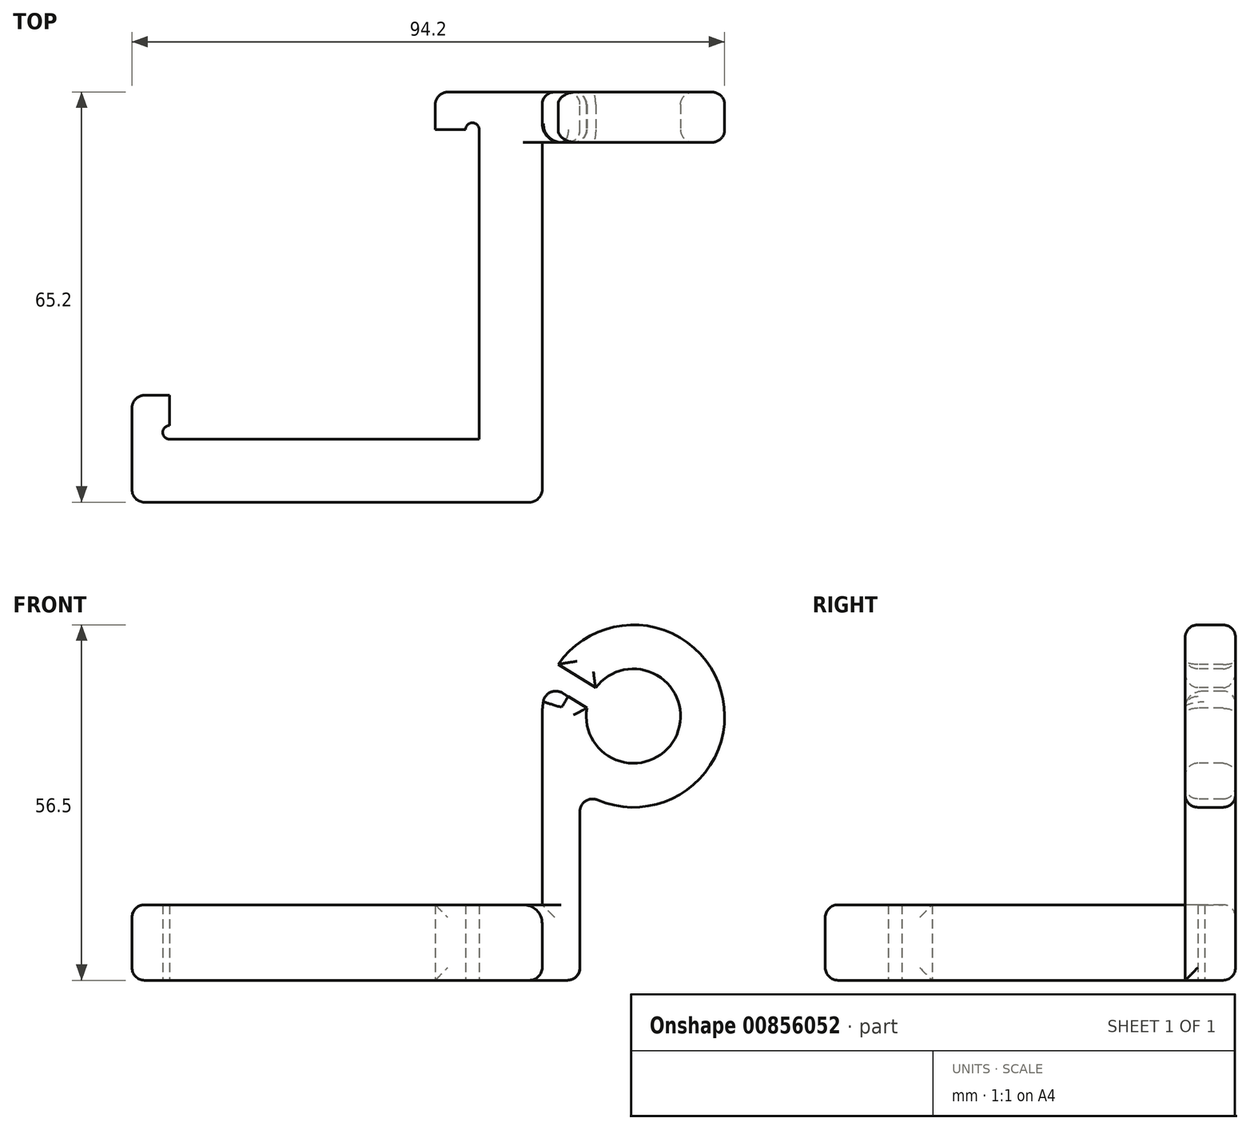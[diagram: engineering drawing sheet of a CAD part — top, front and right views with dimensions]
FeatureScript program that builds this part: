
annotation { "Feature Type Name" : "Feature", "Feature Type Description" : "" }
export const myFeature = defineFeature(function(context is Context, id is Id, definition is map)
    precondition{}
    {
        {
            var Q0;
            Q0=qCreatedBy(makeId("Top.planeOp"),FACE);
            var sketch = newSketch(context, id + "F0", { "sketchPlane" : qUnion([Q0])});
            skLineSegment(sketch, "E0.bottom", {"start": v(0, 0) * mm, "end": v(65.2, 0) * mm});
            skLineSegment(sketch, "E0.top", {"start": v(0, 17) * mm, "end": v(6, 17) * mm});
            skLineSegment(sketch, "E0.left", {"start": v(0, 0) * mm, "end": v(0, 17) * mm});
            skLineSegment(sketch, "E0.right", {"start": v(65.2, 0) * mm, "end": v(65.2, 65.2) * mm});
            skLineSegment(sketch, "E1.top", {"start": v(6, 10) * mm, "end": v(55.2, 10) * mm});
            skLineSegment(sketch, "E1.left", {"start": v(6, 17) * mm, "end": v(6, 10) * mm});
            skLineSegment(sketch, "E1.right", {"start": v(55.2, 59.2) * mm, "end": v(55.2, 10) * mm});
            skLineSegment(sketch, "E2.bottom", {"start": v(65.2, 65.2) * mm, "end": v(48.2, 65.2) * mm});
            skLineSegment(sketch, "E2.top", {"start": v(55.2, 59.2) * mm, "end": v(48.2, 59.2) * mm});
            skLineSegment(sketch, "E2.left", {"start": v(65.2, 65.2) * mm, "end": v(65.2, 59.2) * mm});
            skLineSegment(sketch, "E2.right", {"start": v(48.2, 65.2) * mm, "end": v(48.2, 59.2) * mm});
            skSolve(sketch);
        }
        {
            var Q0;
            Q0=qSketchRegion(id+"F0",true);
            extrude(context, id + "F1", {"entities" : qUnion([Q0]), "depth" : 12 * mm, "offsetDistance" : 25 * mm});
        }
        {
            var Q0;
            Q0=qCreatedBy(makeId("Top.planeOp"),FACE);
            var sketch = newSketch(context, id + "F2", { "sketchPlane" : qUnion([Q0])});
            skCircle(sketch, "E3", {"center": v(6, 11.1) * mm, "radius": 1.1 * mm});
            skCircle(sketch, "E4", {"center": v(54.1, 59.2) * mm, "radius": 1.1 * mm});
            skSolve(sketch);
        }
        {
            var Q0;
            Q0=qSketchRegion(id+"F2",true);
            extrude(context, id + "F3", {"entities" : qUnion([Q0]), "operationType" : NewBodyOperationType.REMOVE, "endBound" : BoundingType.THROUGH_ALL, "depth" : 25 * mm, "offsetDistance" : 25 * mm});
        }
        {
            var Q0;
            Q0=makeQuery(id+"F1.opExtrude","SWEPT_FACE",FACE,{"disambiguationData":[OSD([sQuery(id+"F0.wireOp",EDGE,"E0.right"),sQuery(id+"F0.wireOp",EDGE,"E2.left")])]});
            var sketch = newSketch(context, id + "F4", { "sketchPlane" : qUnion([Q0])});
            skLineSegment(sketch, "E5.bottom", {"start": v(65.2, 0) * mm, "end": v(57.2, 0) * mm});
            skLineSegment(sketch, "E5.top", {"start": v(65.2, 42) * mm, "end": v(57.2, 42) * mm});
            skLineSegment(sketch, "E5.left", {"start": v(65.2, 0) * mm, "end": v(65.2, 42) * mm});
            skLineSegment(sketch, "E5.right", {"start": v(57.2, 0) * mm, "end": v(57.2, 42) * mm});
            skSolve(sketch);
        }
        {
            var Q0;
            Q0 = qSketchRegion(id + "F4", true);
            extrude(context, id + "F5", {"entities" : qUnion([Q0]), "operationType" : NewBodyOperationType.ADD, "depth" : 6 * mm, "offsetDistance" : 25 * mm});
        }
        {
            var Q0;
            Q0=makeQuery(id+"F5.opExtrude","SWEPT_FACE",FACE,{"disambiguationData":[OSD([sQuery(id+"F4.wireOp",EDGE,"E5.right")])]});
            var sketch = newSketch(context, id + "F6", { "sketchPlane" : qUnion([Q0])});
            skArc(sketch, "E6", {"start": v(66.12, 47.1) * mm, "mid": v(92.56, 35.3) * mm, "end": v(67.75, 50.2) * mm});
            skArc(sketch, "E7", {"start": v(72.3, 43.25) * mm, "mid": v(86.6, 39.04) * mm, "end": v(73.7, 46.5) * mm});
            skLineSegment(sketch, "E8", {"start": v(72.3, 43.25) * mm, "end": v(66.12, 47.1) * mm});
            skLineSegment(sketch, "E9", {"start": v(73.7, 46.5) * mm, "end": v(67.75, 50.2) * mm});
            skSolve(sketch);
        }
        {
            var Q0;
            Q0 = qSketchRegion(id + "F6", true);
            var Q1;
            Q1=makeQuery(id+"F5.boolean.opBoolean","MERGE",FACE,{"derivedFrom":[makeQuery(id+"F1.opExtrude","SWEPT_FACE",FACE,{"disambiguationData":[OSD([sQuery(id+"F0.wireOp",EDGE,"E2.bottom")])]}),makeQuery(id+"F5.opExtrude","SWEPT_FACE",FACE,{"disambiguationData":[OSD([sQuery(id+"F4.wireOp",EDGE,"E5.left")])]})]});
            extrude(context, id + "F7", {"entities" : qUnion([Q0]), "operationType" : NewBodyOperationType.ADD, "endBound" : BoundingType.UP_TO_SURFACE, "oppositeDirection" : true, "depth" : 6 * mm, "endBoundEntityFace" : qUnion([Q1]), "offsetDistance" : 25 * mm});
        }
        {
            var Q0;
            {var subQ0=sQuery(id+"F0.wireOp",EDGE,"E2.left");var subQ1=sQuery(id+"F0.wireOp",EDGE,"E0.right");Q0=makeQuery(id+"F5.boolean.opBoolean","SPLIT",EDGE,{"disambiguationData":[topologyDisambiguationEdgeConnected([makeQuery(id+"F5.opExtrude","CAP_FACE",FACE,{"disambiguationData":[OSD([sQuery(id+"F4.wireOp",EDGE,"E5.bottom"),sQuery(id+"F4.wireOp",EDGE,"E5.top"),sQuery(id+"F4.wireOp",EDGE,"E5.left"),sQuery(id+"F4.wireOp",EDGE,"E5.right")])],"isStart":true})])],"derivedFrom":makeQuery(id+"F1.opExtrude","CAP_EDGE",EDGE,{"disambiguationData":[OSD([subQ1,subQ0])],"isStart":false})});}
            fillet(context, id + "F8", {"entities" : qUnion([Q0]), "radius" : 3 * mm, "tangentPropagation" : true, "allowEdgeOverflow" : false});
        }
        {
            var Q0;
            {var subQ0=sQuery(id+"F4.wireOp",EDGE,"E5.right");var subQ1=sQuery(id+"F0.wireOp",EDGE,"E2.left");var subQ2=sQuery(id+"F0.wireOp",EDGE,"E0.right");Q0=makeQuery(id+"F8.opFillet","TWEAK_EDGE",EDGE,{"derivedFrom":[makeQuery(id+"F5.boolean.opBoolean","TWEAK_VERTEX",VERTEX,{"derivedFrom":[makeQuery(id+"F1.opExtrude","SWEPT_FACE",FACE,{"disambiguationData":[OSD([subQ2,subQ1])]}),makeQuery(id+"F1.opExtrude","CAP_FACE",FACE,{"disambiguationData":[OSD([sQuery(id+"F0.wireOp",EDGE,"E0.bottom"),sQuery(id+"F0.wireOp",EDGE,"E0.top"),sQuery(id+"F0.wireOp",EDGE,"E0.left"),subQ2,sQuery(id+"F0.wireOp",EDGE,"E1.top"),sQuery(id+"F0.wireOp",EDGE,"E1.left"),sQuery(id+"F0.wireOp",EDGE,"E1.right"),sQuery(id+"F0.wireOp",EDGE,"E2.bottom"),sQuery(id+"F0.wireOp",EDGE,"E2.top"),subQ1,sQuery(id+"F0.wireOp",EDGE,"E2.right")])],"isStart":false}),makeQuery(id+"F5.opExtrude","CAP_FACE",FACE,{"disambiguationData":[OSD([sQuery(id+"F4.wireOp",EDGE,"E5.bottom"),sQuery(id+"F4.wireOp",EDGE,"E5.top"),sQuery(id+"F4.wireOp",EDGE,"E5.left"),subQ0])],"isStart":true}),makeQuery(id+"F5.opExtrude","SWEPT_FACE",FACE,{"disambiguationData":[OSD([subQ0])]})]})]});}
            var Q1;
            {var subQ0=sQuery(id+"F4.wireOp",EDGE,"E5.right");Q1=makeQuery(id+"F5.boolean.opBoolean","SPLIT",EDGE,{"disambiguationData":[topologyDisambiguationEdgeConnected([makeQuery(id+"F1.opExtrude","SWEPT_FACE",FACE,{"disambiguationData":[OSD([sQuery(id+"F0.wireOp",EDGE,"E0.right"),sQuery(id+"F0.wireOp",EDGE,"E2.left")])]})])],"derivedFrom":makeQuery(id+"F5.opExtrude","CAP_EDGE",EDGE,{"disambiguationData":[OSD([subQ0])],"isStart":true})});}
            fillet(context, id + "F9", {"entities" : qUnion([Q0, Q1]), "radius" : 3 * mm, "tangentPropagation" : true, "allowEdgeOverflow" : false});
        }
        {
            var Q0;
            Q0=makeQuery(id+"F1.opExtrude","SWEPT_FACE",FACE,{"disambiguationData":[OSD([sQuery(id+"F0.wireOp",EDGE,"E0.left")])]});
            var Q1;
            Q1=makeQuery(id+"F1.opExtrude","SWEPT_FACE",FACE,{"disambiguationData":[OSD([sQuery(id+"F0.wireOp",EDGE,"E0.bottom")])]});
            var Q2;
            {var subQ0=sQuery(id+"F4.wireOp",EDGE,"E5.left");var subQ1=sQuery(id+"F0.wireOp",EDGE,"E2.bottom");Q2=makeQuery(id+"F7.boolean.opBoolean","MERGE",FACE,{"derivedFrom":[makeQuery(id+"F5.boolean.opBoolean","MERGE",FACE,{"derivedFrom":[makeQuery(id+"F1.opExtrude","SWEPT_FACE",FACE,{"disambiguationData":[OSD([subQ1])]}),makeQuery(id+"F5.opExtrude","SWEPT_FACE",FACE,{"disambiguationData":[OSD([subQ0])]})]}),makeQuery(id+"F7.opExtrude","CAP_FACE",FACE,{"disambiguationData":[OSD([subQ1,subQ0])],"isStart":false})]});}
            var Q3;
            {var subQ0=sQuery(id+"F4.wireOp",EDGE,"E5.right");Q3=makeQuery(id+"F5.boolean.opBoolean","SPLIT",EDGE,{"disambiguationData":[topologyDisambiguationEdgeConnected([makeQuery(id+"F5.opExtrude","CAP_FACE",FACE,{"disambiguationData":[OSD([sQuery(id+"F4.wireOp",EDGE,"E5.bottom"),sQuery(id+"F4.wireOp",EDGE,"E5.top"),sQuery(id+"F4.wireOp",EDGE,"E5.left"),subQ0])],"isStart":true})])],"derivedFrom":makeQuery(id+"F5.opExtrude","CAP_EDGE",EDGE,{"disambiguationData":[OSD([subQ0])],"isStart":true})});}
            var Q4;
            Q4=makeQuery(id+"F5.opExtrude","CAP_EDGE",EDGE,{"disambiguationData":[OSD([sQuery(id+"F4.wireOp",EDGE,"E5.right")])],"isStart":false});
            var Q5;
            {var subQ0=sQuery(id+"F6.wireOp",EDGE,"E9");var subQ1=sQuery(id+"F6.wireOp",EDGE,"E6");Q5=makeQuery(id+"F7.boolean.opBoolean","SPLIT",EDGE,{"disambiguationData":[TD([makeQuery(id+"F7.opExtrude","SWEPT_FACE",FACE,{"disambiguationData":[OSD([subQ0])]})])],"derivedFrom":makeQuery(id+"F7.opExtrude","CAP_EDGE",EDGE,{"disambiguationData":[OSD([subQ1])],"isStart":true})});}
            var Q6;
            Q6=makeQuery(id+"F7.opExtrude","CAP_EDGE",EDGE,{"disambiguationData":[OSD([sQuery(id+"F6.wireOp",EDGE,"E7")])],"isStart":true});
            var Q7;
            Q7=makeQuery(id+"F1.opExtrude","CAP_EDGE",EDGE,{"disambiguationData":[OSD([sQuery(id+"F0.wireOp",EDGE,"E0.right"),sQuery(id+"F0.wireOp",EDGE,"E2.left")])],"isStart":true});
            var Q8;
            Q8=makeQuery(id+"F7.opExtrude","CAP_EDGE",EDGE,{"disambiguationData":[OSD([sQuery(id+"F6.wireOp",EDGE,"E9")])],"isStart":true});
            var Q9;
            Q9=makeQuery(id+"F7.opExtrude","CAP_EDGE",EDGE,{"disambiguationData":[OSD([sQuery(id+"F6.wireOp",EDGE,"E8")])],"isStart":true});
            var Q10;
            {var subQ0=sQuery(id+"F0.wireOp",EDGE,"E2.left");var subQ1=sQuery(id+"F0.wireOp",EDGE,"E0.right");Q10=makeQuery(id+"F5.boolean.opBoolean","SPLIT",EDGE,{"disambiguationData":[topologyDisambiguationEdgeConnected([makeQuery(id+"F1.opExtrude","SWEPT_FACE",FACE,{"disambiguationData":[OSD([subQ1,subQ0])]})])],"derivedFrom":makeQuery(id+"F1.opExtrude","CAP_EDGE",EDGE,{"disambiguationData":[OSD([subQ1,subQ0])],"isStart":false})});}
            var Q11;
            Q11=makeQuery(id+"F5.opExtrude","CAP_EDGE",EDGE,{"disambiguationData":[OSD([sQuery(id+"F4.wireOp",EDGE,"E5.bottom")])],"isStart":false});
            var Q12;
            Q12=makeQuery(id+"F7.boolean.opBoolean","INTERSECT",EDGE,{"derivedFrom":[makeQuery(id+"F5.opExtrude","CAP_FACE",FACE,{"disambiguationData":[OSD([sQuery(id+"F4.wireOp",EDGE,"E5.bottom"),sQuery(id+"F4.wireOp",EDGE,"E5.top"),sQuery(id+"F4.wireOp",EDGE,"E5.left"),sQuery(id+"F4.wireOp",EDGE,"E5.right")])],"isStart":false}),makeQuery(id+"F7.opExtrude","SWEPT_FACE",FACE,{"disambiguationData":[OSD([sQuery(id+"F6.wireOp",EDGE,"E6")])]})]});
            fillet(context, id + "F10", {"entities" : qUnion([Q0, Q1, Q2, Q3, Q4, Q5, Q6, Q7, Q8, Q9, Q10, Q11, Q12]), "radius" : 2 * mm, "tangentPropagation" : true, "allowEdgeOverflow" : false});
        }
    });
